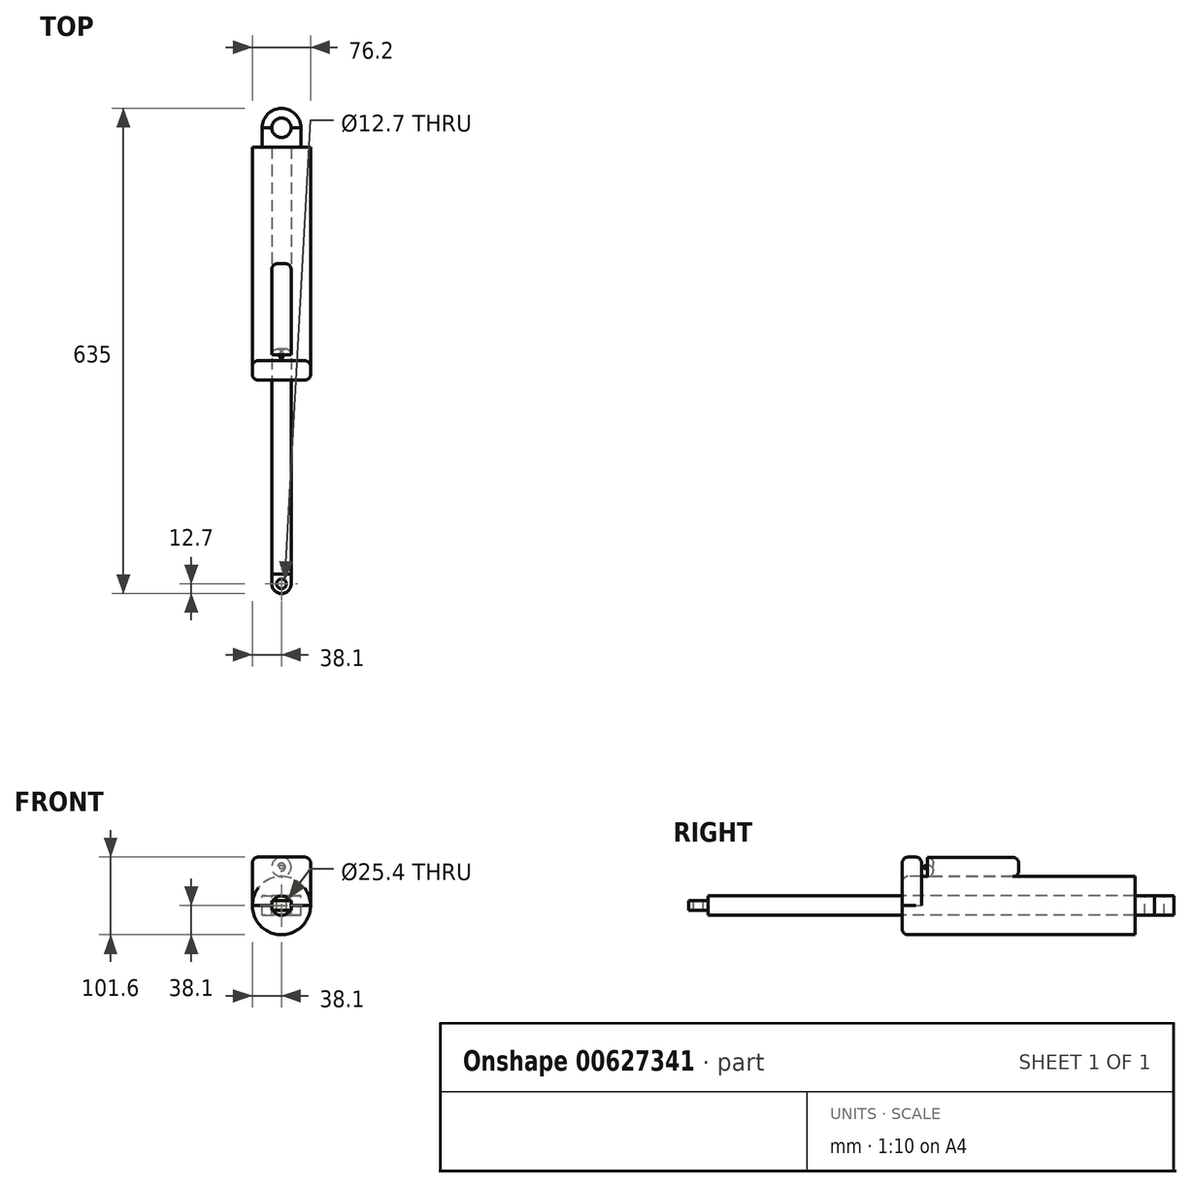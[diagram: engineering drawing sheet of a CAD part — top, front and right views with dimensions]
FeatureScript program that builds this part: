
annotation { "Feature Type Name" : "Feature", "Feature Type Description" : "" }
export const myFeature = defineFeature(function(context is Context, id is Id, definition is map)
    precondition{}
    {
        {
            var Q0;
            Q0=qCreatedBy(makeId("Front.planeOp"),FACE);
            var sketch = newSketch(context, id + "F0", { "sketchPlane" : qUnion([Q0])});
            skCircle(sketch, "E0", {"center": v(0, 0) * mm, "radius": 38.1 * mm});
            skCircle(sketch, "E1", {"center": v(0, 0) * mm, "radius": 12.7 * mm});
            skSolve(sketch);
        }
        {
            var Q0;
            Q0=makeQuery(id+"F0.imprint","IMPRINT",FACE,{"disambiguationData":[TD([[makeQuery(id+"F0.imprint","IMPRINT",EDGE,{"derivedFrom":sQuery(id+"F0.wireOp",EDGE,"E1")}),1.0]])]});
            extrude(context, id + "F1", {"entities" : qUnion([Q0]), "depth" : 254 * mm, "offsetDistance" : 25.4 * mm});
        }
        {
            var Q0;
            Q0 = qSketchRegion(id + "F0", true);
            extrude(context, id + "F2", {"entities" : qUnion([Q0]), "oppositeDirection" : true, "depth" : 304.8 * mm, "offsetDistance" : 25.4 * mm});
        }
        {
            var Q0;
            Q0=qCreatedBy(makeId("Front.planeOp"),FACE);
            var sketch = newSketch(context, id + "F3", { "sketchPlane" : qUnion([Q0])});
            skLineSegment(sketch, "E2.bottom", {"start": v(0, 0) * mm, "end": v(38.1, 0) * mm});
            skLineSegment(sketch, "E2.top", {"start": v(0, 63.5) * mm, "end": v(38.1, 63.5) * mm});
            skLineSegment(sketch, "E2.left", {"start": v(0, 0) * mm, "end": v(0, 63.5) * mm});
            skLineSegment(sketch, "E2.right", {"start": v(38.1, 0) * mm, "end": v(38.1, 63.5) * mm});
            skLineSegment(sketch, "E3.bottom", {"start": v(0, 0) * mm, "end": v(-38.1, 0) * mm});
            skLineSegment(sketch, "E3.top", {"start": v(0, 63.5) * mm, "end": v(-38.1, 63.5) * mm});
            skLineSegment(sketch, "E3.right", {"start": v(-38.1, 0) * mm, "end": v(-38.1, 63.5) * mm});
            skSolve(sketch);
        }
        {
            var Q0;
            Q0 = qSketchRegion(id + "F3", true);
            extrude(context, id + "F4", {"entities" : qUnion([Q0]), "oppositeDirection" : true, "depth" : 25.4 * mm, "offsetDistance" : 25.4 * mm});
        }
        {
            var Q0;
            Q0=makeQuery(id+"F4.opExtrude","CAP_FACE",FACE,{"disambiguationData":[OSD([sQuery(id+"F3.wireOp",EDGE,"E2.bottom"),sQuery(id+"F3.wireOp",EDGE,"E2.top"),sQuery(id+"F3.wireOp",EDGE,"E2.right"),sQuery(id+"F3.wireOp",EDGE,"E3.bottom"),sQuery(id+"F3.wireOp",EDGE,"E3.top"),sQuery(id+"F3.wireOp",EDGE,"E3.right")])],"isStart":false});
            var sketch = newSketch(context, id + "F5", { "sketchPlane" : qUnion([Q0])});
            skCircle(sketch, "E4", {"center": v(0, 50.5) * mm, "radius": 12.7 * mm});
            skSolve(sketch);
        }
        {
            var Q0;
            Q0=makeQuery(id+"F5.imprint","IMPRINT",FACE,{"disambiguationData":[TD([[makeQuery(id+"F5.imprint","IMPRINT",EDGE,{"derivedFrom":sQuery(id+"F5.wireOp",EDGE,"E4")}),1.0]])]});
            extrude(context, id + "F6", {"entities" : qUnion([Q0]), "depth" : 127 * mm, "offsetDistance" : 25.4 * mm});
        }
        {
            var Q0;
            Q0=makeQuery(id+"F1.opExtrude","CAP_FACE",FACE,{"disambiguationData":[OSD([sQuery(id+"F0.wireOp",EDGE,"E1")])],"isStart":true});
            extrude(context, id + "F7", {"entities" : qUnion([Q0]), "depth" : 304.8 * mm, "offsetDistance" : 25.4 * mm});
        }
        {
            var Q0;
            Q0=makeQuery(id+"F2.opExtrude","CAP_FACE",FACE,{"disambiguationData":[OSD([sQuery(id+"F0.wireOp",EDGE,"E0"),sQuery(id+"F0.wireOp",EDGE,"E1")])],"isStart":false});
            var sketch = newSketch(context, id + "F8", { "sketchPlane" : qUnion([Q0])});
            skLineSegment(sketch, "E5.bottom", {"start": v(25.4, -12.7) * mm, "end": v(-25.4, -12.7) * mm});
            skLineSegment(sketch, "E5.top", {"start": v(25.4, 12.7) * mm, "end": v(-25.4, 12.7) * mm});
            skLineSegment(sketch, "E5.left", {"start": v(25.4, -12.7) * mm, "end": v(25.4, 12.7) * mm});
            skLineSegment(sketch, "E5.right", {"start": v(-25.4, -12.7) * mm, "end": v(-25.4, 12.7) * mm});
            skPoint(sketch, "E5.middle", {"position": v(0, 0) * mm});
            skSolve(sketch);
        }
        {
            var Q0;
            Q0 = qSketchRegion(id + "F8", true);
            extrude(context, id + "F9", {"entities" : qUnion([Q0]), "depth" : 25.4 * mm, "offsetDistance" : 25.4 * mm});
        }
        {
            var Q0;
            Q0=makeQuery(id+"F9.opExtrude","SWEPT_FACE",FACE,{"disambiguationData":[OSD([sQuery(id+"F8.wireOp",EDGE,"E5.top")])]});
            var sketch = newSketch(context, id + "F10", { "sketchPlane" : qUnion([Q0])});
            skArc(sketch, "E6", {"start": v(25.4, 330.2) * mm, "mid": v(0, 355.6) * mm, "end": v(-25.4, 330.2) * mm});
            skSolve(sketch);
        }
        {
            var Q0;
            Q0=makeQuery(id+"F10.imprint","IMPRINT",FACE,{"disambiguationData":[TD([[makeQuery(id+"F10.imprint","IMPRINT",EDGE,{"derivedFrom":sQuery(id+"F10.wireOp",EDGE,"E6")}),1.0]])]});
            extrude(context, id + "F11", {"entities" : qUnion([Q0]), "oppositeDirection" : true, "depth" : 25.4 * mm, "offsetDistance" : 25.4 * mm});
        }
        {
            var Q0;
            Q0=makeQuery(id+"F11.opExtrude","CAP_FACE",FACE,{"disambiguationData":[OSD([sQuery(id+"F8.wireOp",EDGE,"E5.top"),sQuery(id+"F10.wireOp",EDGE,"E6")])],"isStart":true});
            var sketch = newSketch(context, id + "F12", { "sketchPlane" : qUnion([Q0])});
            skPoint(sketch, "E7", {"position": v(0, 330.2) * mm});
            skSolve(sketch);
        }
        {
            var Q0;
            Q0=sQuery(id+"F12.wireOp",VERTEX,"E7");
            var Q1;
            Q1=makeQuery(id+"F9.opExtrude","SWEPT_BODY",BODY,{"disambiguationData":[OSD([sQuery(id+"F8.wireOp",EDGE,"E5.bottom"),sQuery(id+"F8.wireOp",EDGE,"E5.top"),sQuery(id+"F8.wireOp",EDGE,"E5.left"),sQuery(id+"F8.wireOp",EDGE,"E5.right")])]});
            var Q2;
            Q2=makeQuery(id+"F11.opExtrude","SWEPT_BODY",BODY,{"disambiguationData":[OSD([sQuery(id+"F8.wireOp",EDGE,"E5.top"),sQuery(id+"F10.wireOp",EDGE,"E6")])]});
            hole(context, id + "F13", {"style" : HoleStyle.SIMPLE, "endStyle" : HoleEndStyle.THROUGH, "holeDiameter" : 25.4 * mm, "majorDiameter" : 6.35 * mm, "isTappedThrough" : true, "tappedDepth" : 12.7 * mm, "tapClearance" : 3, "locations" : qUnion([Q0]), "scope" : qUnion([Q1, Q2])});
        }
        {
            var Q0;
            Q0=makeQuery(id+"F4.opExtrude","SWEPT_EDGE",EDGE,{"disambiguationData":[OSD([sQuery(id+"F3.wireOp",EDGE,"E2.top"),sQuery(id+"F3.wireOp",EDGE,"E2.right")])]});
            var Q1;
            Q1=makeQuery(id+"F4.opExtrude","CAP_EDGE",EDGE,{"disambiguationData":[OSD([sQuery(id+"F3.wireOp",EDGE,"E2.top"),sQuery(id+"F3.wireOp",EDGE,"E3.top")])],"isStart":false});
            var Q2;
            Q2=makeQuery(id+"F4.opExtrude","SWEPT_EDGE",EDGE,{"disambiguationData":[OSD([sQuery(id+"F3.wireOp",EDGE,"E3.top"),sQuery(id+"F3.wireOp",EDGE,"E3.right")])]});
            var Q3;
            Q3=makeQuery(id+"F4.opExtrude","CAP_EDGE",EDGE,{"disambiguationData":[OSD([sQuery(id+"F3.wireOp",EDGE,"E2.top"),sQuery(id+"F3.wireOp",EDGE,"E3.top")])],"isStart":true});
            var Q4;
            Q4=makeQuery(id+"F4.opExtrude","CAP_EDGE",EDGE,{"disambiguationData":[OSD([sQuery(id+"F3.wireOp",EDGE,"E2.right")])],"isStart":false});
            var Q5;
            Q5=makeQuery(id+"F4.opExtrude","CAP_EDGE",EDGE,{"disambiguationData":[OSD([sQuery(id+"F3.wireOp",EDGE,"E2.right")])],"isStart":true});
            var Q6;
            Q6=makeQuery(id+"F6.opExtrude","CAP_EDGE",EDGE,{"disambiguationData":[OSD([sQuery(id+"F5.wireOp",EDGE,"E4")])],"isStart":true});
            var Q7;
            Q7=makeQuery(id+"F6.opExtrude","CAP_EDGE",EDGE,{"disambiguationData":[OSD([sQuery(id+"F5.wireOp",EDGE,"E4")])],"isStart":false});
            var Q8;
            Q8=makeQuery(id+"F4.opExtrude","CAP_EDGE",EDGE,{"disambiguationData":[OSD([sQuery(id+"F3.wireOp",EDGE,"E3.right")])],"isStart":false});
            var Q9;
            Q9=makeQuery(id+"F4.opExtrude","CAP_EDGE",EDGE,{"disambiguationData":[OSD([sQuery(id+"F3.wireOp",EDGE,"E3.right")])],"isStart":true});
            var Q10;
            Q10=makeQuery(id+"F2.opExtrude","CAP_EDGE",EDGE,{"disambiguationData":[OSD([sQuery(id+"F0.wireOp",EDGE,"E0")])],"isStart":true});
            fillet(context, id + "F14", {"entities" : qUnion([Q0, Q1, Q2, Q3, Q4, Q5, Q6, Q7, Q8, Q9, Q10]), "radius" : 7.62 * mm, "tangentPropagation" : true, "allowEdgeOverflow" : false});
        }
        {
            var Q0;
            Q0=makeQuery(id+"F1.opExtrude","CAP_FACE",FACE,{"disambiguationData":[OSD([sQuery(id+"F0.wireOp",EDGE,"E1")])],"isStart":false});
            var sketch = newSketch(context, id + "F15", { "sketchPlane" : qUnion([Q0])});
            skLineSegment(sketch, "E8.bottom", {"start": v(12.7, 0) * mm, "end": v(-12.7, 0) * mm});
            skLineSegment(sketch, "E8.top", {"start": v(12.7, 0) * mm, "end": v(-12.7, 0) * mm});
            skLineSegment(sketch, "E8.left", {"start": v(12.7, 0) * mm, "end": v(12.7, 0) * mm});
            skLineSegment(sketch, "E8.right", {"start": v(-12.7, 0) * mm, "end": v(-12.7, 0) * mm});
            skPoint(sketch, "E8.middle", {"position": v(0, 0) * mm});
            skLineSegment(sketch, "E9.bottom", {"start": v(12.7, -6.35) * mm, "end": v(-12.7, -6.35) * mm});
            skLineSegment(sketch, "E9.top", {"start": v(12.7, 6.35) * mm, "end": v(-12.7, 6.35) * mm});
            skLineSegment(sketch, "E9.left", {"start": v(12.7, -6.35) * mm, "end": v(12.7, 6.35) * mm});
            skLineSegment(sketch, "E9.right", {"start": v(-12.7, -6.35) * mm, "end": v(-12.7, 6.35) * mm});
            skSolve(sketch);
        }
        {
            var Q0;
            Q0 = qSketchRegion(id + "F15", true);
            extrude(context, id + "F16", {"entities" : qUnion([Q0]), "operationType" : NewBodyOperationType.ADD, "depth" : 12.7 * mm, "offsetDistance" : 25.4 * mm});
        }
        {
            var Q0;
            Q0=makeQuery(id+"F16.opExtrude","SWEPT_FACE",FACE,{"disambiguationData":[OSD([sQuery(id+"F15.wireOp",EDGE,"E9.top")])]});
            var sketch = newSketch(context, id + "F17", { "sketchPlane" : qUnion([Q0])});
            skArc(sketch, "E10", {"start": v(-12.7, -266.7) * mm, "mid": v(0, -279.4) * mm, "end": v(12.7, -266.7) * mm});
            skSolve(sketch);
        }
        {
            var Q0;
            Q0=makeQuery(id+"F17.imprint","IMPRINT",FACE,{"disambiguationData":[TD([[makeQuery(id+"F17.imprint","IMPRINT",EDGE,{"derivedFrom":sQuery(id+"F17.wireOp",EDGE,"E10")}),1.0]])]});
            extrude(context, id + "F18", {"entities" : qUnion([Q0]), "operationType" : NewBodyOperationType.ADD, "oppositeDirection" : true, "depth" : 12.7 * mm, "offsetDistance" : 25.4 * mm});
        }
        {
            var Q0;
            {var subQ0=sQuery(id+"F15.wireOp",EDGE,"E9.top");Q0=makeQuery(id+"F18.boolean.opBoolean","MERGE",FACE,{"derivedFrom":[makeQuery(id+"F16.opExtrude","SWEPT_FACE",FACE,{"disambiguationData":[OSD([subQ0])]}),makeQuery(id+"F18.opExtrude","CAP_FACE",FACE,{"disambiguationData":[OSD([subQ0,sQuery(id+"F17.wireOp",EDGE,"E10")])],"isStart":true})]});}
            var sketch = newSketch(context, id + "F19", { "sketchPlane" : qUnion([Q0])});
            skPoint(sketch, "E11", {"position": v(0, -266.7) * mm});
            skSolve(sketch);
        }
        {
            var Q0;
            Q0=sQuery(id+"F19.wireOp",VERTEX,"E11");
            var Q1;
            Q1=makeQuery(id+"F1.opExtrude","SWEPT_BODY",BODY,{"disambiguationData":[OSD([sQuery(id+"F0.wireOp",EDGE,"E1")])]});
            hole(context, id + "F20", {"style" : HoleStyle.SIMPLE, "endStyle" : HoleEndStyle.THROUGH, "holeDiameter" : 12.7 * mm, "majorDiameter" : 6.35 * mm, "isTappedThrough" : true, "tappedDepth" : 12.7 * mm, "tapClearance" : 3, "locations" : qUnion([Q0]), "scope" : qUnion([Q1])});
        }
    });
